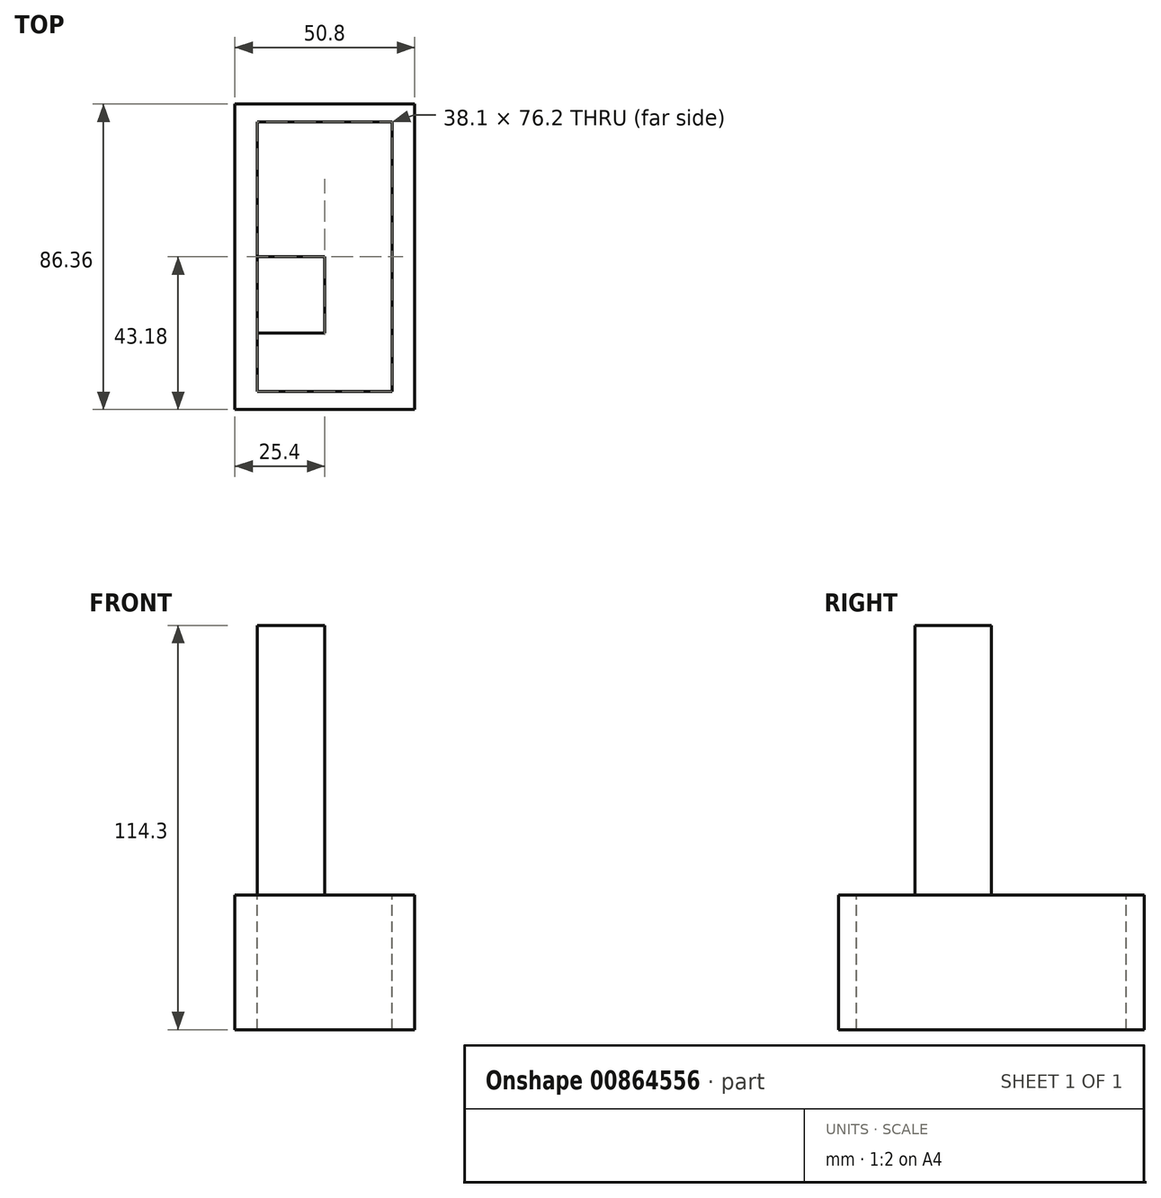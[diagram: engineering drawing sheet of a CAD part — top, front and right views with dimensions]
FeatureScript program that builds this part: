
annotation { "Feature Type Name" : "Feature", "Feature Type Description" : "" }
export const myFeature = defineFeature(function(context is Context, id is Id, definition is map)
    precondition{}
    {
        {
            var Q0;
            Q0=qCreatedBy(makeId("Top.planeOp"),FACE);
            var sketch = newSketch(context, id + "F0", { "sketchPlane" : qUnion([Q0])});
            skLineSegment(sketch, "E0.bottom", {"start": v(25.4, -43.18) * mm, "end": v(-25.4, -43.18) * mm});
            skLineSegment(sketch, "E0.top", {"start": v(25.4, 43.18) * mm, "end": v(-25.4, 43.18) * mm});
            skLineSegment(sketch, "E0.left", {"start": v(25.4, -43.18) * mm, "end": v(25.4, 43.18) * mm});
            skLineSegment(sketch, "E0.right", {"start": v(-25.4, -43.18) * mm, "end": v(-25.4, 43.18) * mm});
            skPoint(sketch, "E0.middle", {"position": v(0, 0) * mm});
            skSolve(sketch);
        }
        {
            var Q0;
            Q0=makeQuery(id+"F0.imprint","IMPRINT",FACE,{"disambiguationData":[TD([[makeQuery(id+"F0.imprint","IMPRINT",EDGE,{"derivedFrom":sQuery(id+"F0.wireOp",EDGE,"E0.bottom")}),-1.0]])]});
            extrude(context, id + "F1", {"entities" : qUnion([Q0]), "depth" : 25.4 * mm, "offsetDistance" : 25.4 * mm});
        }
        {
            var Q0;
            Q0=makeQuery(id+"F1.opExtrude","CAP_FACE",FACE,{"disambiguationData":[OSD([sQuery(id+"F0.wireOp",EDGE,"E0.bottom"),sQuery(id+"F0.wireOp",EDGE,"E0.top"),sQuery(id+"F0.wireOp",EDGE,"E0.left"),sQuery(id+"F0.wireOp",EDGE,"E0.right")])],"isStart":false});
            var sketch = newSketch(context, id + "F2", { "sketchPlane" : qUnion([Q0])});
            skLineSegment(sketch, "E1", {"start": v(-25.4, 43.18) * mm, "end": v(25.4, 43.18) * mm});
            skLineSegment(sketch, "E2", {"start": v(25.4, 43.18) * mm, "end": v(19.05, 43.18) * mm});
            skLineSegment(sketch, "E3", {"start": v(-25.4, 43.18) * mm, "end": v(-25.4, -43.18) * mm});
            skLineSegment(sketch, "E4", {"start": v(-25.4, -43.18) * mm, "end": v(-19.05, -43.18) * mm});
            skLineSegment(sketch, "E5", {"start": v(-19.05, -43.18) * mm, "end": v(-19.05, 43.18) * mm});
            skLineSegment(sketch, "E6", {"start": v(-19.05, 43.18) * mm, "end": v(-19.05, 38.1) * mm});
            skLineSegment(sketch, "E7", {"start": v(-19.05, 38.1) * mm, "end": v(-25.4, 38.1) * mm});
            skLineSegment(sketch, "E8", {"start": v(-25.4, 38.1) * mm, "end": v(25.4, 38.1) * mm});
            skLineSegment(sketch, "E9", {"start": v(25.4, 38.1) * mm, "end": v(25.4, -43.18) * mm});
            skLineSegment(sketch, "E10", {"start": v(25.4, -43.18) * mm, "end": v(-25.4, -43.18) * mm});
            skLineSegment(sketch, "E11", {"start": v(-25.4, -37.8) * mm, "end": v(-25.4, -43.18) * mm});
            skLineSegment(sketch, "E12", {"start": v(-25.4, -43.18) * mm, "end": v(-25.4, -38.1) * mm});
            skLineSegment(sketch, "E13", {"start": v(-25.4, -38.1) * mm, "end": v(25.4, -38.1) * mm});
            skLineSegment(sketch, "E14", {"start": v(25.4, -38.1) * mm, "end": v(19.05, -38.1) * mm});
            skLineSegment(sketch, "E15", {"start": v(19.05, -38.1) * mm, "end": v(19.05, 43.18) * mm});
            skSolve(sketch);
        }
        {
            var Q0;
            {var subQ1=sQuery(id+"F2.wireOp",EDGE,"E5");var subQ3=sQuery(id+"F2.wireOp",EDGE,"E13");var subQ4=makeQuery(id+"F2.imprint","INTERSECT",VERTEX,{"derivedFrom":[subQ1,subQ3]});Q0=makeQuery(id+"F2.imprint","IMPRINT",FACE,{"disambiguationData":[TD([[makeQuery(id+"F2.imprint","IMPRINT",EDGE,{"disambiguationData":[TD([[subQ4,-1.0]])],"derivedFrom":subQ1}),-1.0]])]});}
            extrude(context, id + "F3", {"entities" : qUnion([Q0]), "operationType" : NewBodyOperationType.REMOVE, "oppositeDirection" : true, "depth" : 101.6 * mm, "offsetDistance" : 25.4 * mm});
        }
        {
            var Q0;
            Q0=makeQuery(id+"F1.opExtrude","CAP_FACE",FACE,{"disambiguationData":[OSD([sQuery(id+"F0.wireOp",EDGE,"E0.bottom"),sQuery(id+"F0.wireOp",EDGE,"E0.top"),sQuery(id+"F0.wireOp",EDGE,"E0.left"),sQuery(id+"F0.wireOp",EDGE,"E0.right")])],"isStart":false});
            var sketch = newSketch(context, id + "F4", { "sketchPlane" : qUnion([Q0])});
            skLineSegment(sketch, "E16.bottom", {"start": v(25.4, -43.18) * mm, "end": v(-25.4, -43.18) * mm});
            skLineSegment(sketch, "E16.top", {"start": v(25.4, 43.18) * mm, "end": v(-25.4, 43.18) * mm});
            skLineSegment(sketch, "E16.left", {"start": v(25.4, -43.18) * mm, "end": v(25.4, 43.18) * mm});
            skLineSegment(sketch, "E16.right", {"start": v(-25.4, -43.18) * mm, "end": v(-25.4, 43.18) * mm});
            skSolve(sketch);
        }
        {
            var Q0;
            Q0=makeQuery(id+"F4.imprint","IMPRINT",FACE,{"disambiguationData":[TD([[makeQuery(id+"F4.imprint","IMPRINT",EDGE,{"derivedFrom":makeQuery(id+"F3.boolean.opBoolean","COPY",EDGE,{"derivedFrom":makeQuery(id+"F3.opExtrude","CAP_EDGE",EDGE,{"disambiguationData":[OSD([sQuery(id+"F2.wireOp",EDGE,"E5")])],"isStart":true})})}),-1.0]])]});
            var Q1;
            Q1=makeQuery(id+"F4.imprint","IMPRINT",FACE,{"disambiguationData":[TD([[makeQuery(id+"F4.imprint","IMPRINT",EDGE,{"derivedFrom":sQuery(id+"F4.wireOp",EDGE,"E16.bottom")}),-1.0]])]});
            extrude(context, id + "F5", {"entities" : qUnion([Q0, Q1]), "operationType" : NewBodyOperationType.ADD, "depth" : 12.7 * mm, "offsetDistance" : 25.4 * mm});
        }
        {
            var Q0;
            Q0=makeQuery(id+"F5.opExtrude","CAP_FACE",FACE,{"disambiguationData":[OSD([sQuery(id+"F4.wireOp",EDGE,"E16.bottom"),sQuery(id+"F4.wireOp",EDGE,"E16.top"),sQuery(id+"F4.wireOp",EDGE,"E16.left"),sQuery(id+"F4.wireOp",EDGE,"E16.right")])],"isStart":false});
            var sketch = newSketch(context, id + "F6", { "sketchPlane" : qUnion([Q0])});
            skLineSegment(sketch, "E17", {"start": v(-25.4, 43.18) * mm, "end": v(25.4, 43.18) * mm});
            skLineSegment(sketch, "E18", {"start": v(25.4, 43.18) * mm, "end": v(25.4, -43.18) * mm});
            skLineSegment(sketch, "E19", {"start": v(25.4, -43.18) * mm, "end": v(-25.4, -43.18) * mm});
            skLineSegment(sketch, "E20", {"start": v(-25.4, -43.18) * mm, "end": v(-25.4, 43.18) * mm});
            skLineSegment(sketch, "E21", {"start": v(0, 43.18) * mm, "end": v(0, -43.18) * mm});
            skLineSegment(sketch, "E22", {"start": v(0, -43.18) * mm, "end": v(-25.4, -43.18) * mm});
            skLineSegment(sketch, "E23", {"start": v(-12.7, -43.18) * mm, "end": v(-12.7, 43.18) * mm});
            skLineSegment(sketch, "E24", {"start": v(-12.7, 43.18) * mm, "end": v(-12.7, 0) * mm});
            skLineSegment(sketch, "E25", {"start": v(-12.7, 0) * mm, "end": v(0, 0) * mm});
            skLineSegment(sketch, "E26", {"start": v(0, 0) * mm, "end": v(-25.4, 0) * mm});
            skLineSegment(sketch, "E27", {"start": v(-25.4, 0) * mm, "end": v(-25.4, 43.18) * mm});
            skLineSegment(sketch, "E28", {"start": v(-25.4, 21.6) * mm, "end": v(0, 21.6) * mm});
            skLineSegment(sketch, "E29", {"start": v(0, 21.6) * mm, "end": v(0, -43.18) * mm});
            skLineSegment(sketch, "E30", {"start": v(0, -43.18) * mm, "end": v(0, 0) * mm});
            skLineSegment(sketch, "E31", {"start": v(0, -21.6) * mm, "end": v(-25.4, -21.6) * mm});
            skLineSegment(sketch, "E32", {"start": v(-25.4, -21.6) * mm, "end": v(-25.4, 21.6) * mm});
            skLineSegment(sketch, "E33", {"start": v(0, -21.6) * mm, "end": v(12.7, -21.6) * mm});
            skLineSegment(sketch, "E34", {"start": v(12.7, -21.6) * mm, "end": v(12.7, 0) * mm});
            skLineSegment(sketch, "E35", {"start": v(12.7, 0) * mm, "end": v(12.7, 21.59) * mm});
            skLineSegment(sketch, "E36", {"start": v(12.7, 21.6) * mm, "end": v(0, 21.6) * mm});
            skSolve(sketch);
        }
        {
            var Q0;
            {var subQ2=sQuery(id+"F6.wireOp",EDGE,"E29");Q0=makeQuery(id+"F6.imprint","IMPRINT",FACE,{"disambiguationData":[TD([[makeQuery(id+"F6.imprint","IMPRINT",EDGE,{"derivedFrom":subQ2}),1.0]])]});}
            var Q1;
            {var subQ5=sQuery(id+"F6.wireOp",EDGE,"E29");Q1=makeQuery(id+"F6.imprint","IMPRINT",FACE,{"disambiguationData":[TD([[makeQuery(id+"F6.imprint","IMPRINT",EDGE,{"derivedFrom":subQ5}),-1.0]])]});}
            var Q2;
            {var subQ1=sQuery(id+"F6.wireOp",EDGE,"E23");var subQ3=sQuery(id+"F6.wireOp",EDGE,"E31");var subQ4=makeQuery(id+"F6.imprint","INTERSECT",VERTEX,{"derivedFrom":[subQ1,subQ3]});Q2=makeQuery(id+"F6.imprint","IMPRINT",FACE,{"disambiguationData":[TD([[makeQuery(id+"F6.imprint","IMPRINT",EDGE,{"disambiguationData":[TD([[subQ4,-1.0]])],"derivedFrom":subQ1}),-1.0]])]});}
            var Q3;
            {var subQ1=sQuery(id+"F6.wireOp",EDGE,"E23");var subQ3=sQuery(id+"F6.wireOp",EDGE,"E31");var subQ4=makeQuery(id+"F6.imprint","INTERSECT",VERTEX,{"derivedFrom":[subQ1,subQ3]});Q3=makeQuery(id+"F6.imprint","IMPRINT",FACE,{"disambiguationData":[TD([[makeQuery(id+"F6.imprint","IMPRINT",EDGE,{"disambiguationData":[TD([[subQ4,-1.0]])],"derivedFrom":subQ1}),1.0]])]});}
            var Q4;
            {var subQ1=sQuery(id+"F6.wireOp",EDGE,"E24");var subQ3=sQuery(id+"F6.wireOp",EDGE,"E28");var subQ4=makeQuery(id+"F6.imprint","INTERSECT",VERTEX,{"derivedFrom":[subQ1,subQ3]});Q4=makeQuery(id+"F6.imprint","IMPRINT",FACE,{"disambiguationData":[TD([[makeQuery(id+"F6.imprint","IMPRINT",EDGE,{"disambiguationData":[TD([[subQ4,-1.0]])],"derivedFrom":subQ1}),-1.0]])]});}
            extrude(context, id + "F7", {"entities" : qUnion([Q0, Q1, Q2, Q3, Q4]), "operationType" : NewBodyOperationType.ADD, "depth" : 76.2 * mm, "offsetDistance" : 25.4 * mm});
        }
    });
